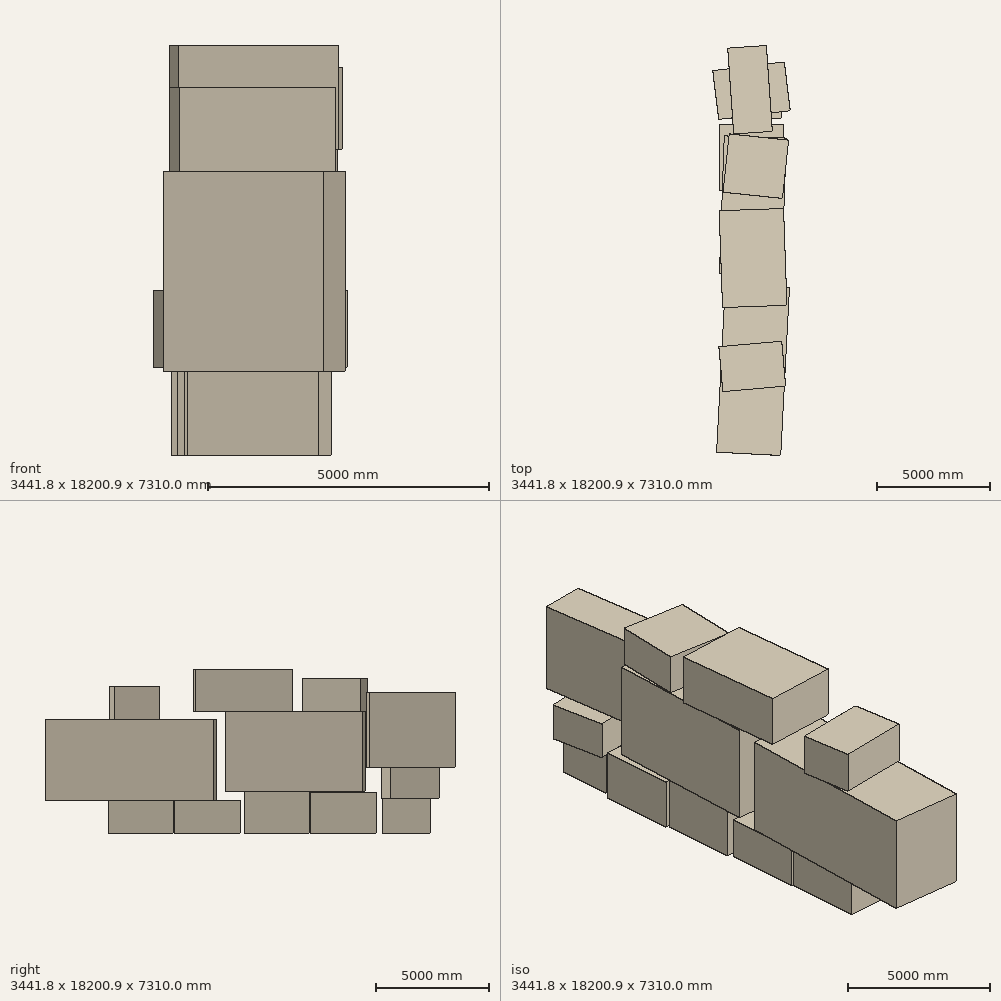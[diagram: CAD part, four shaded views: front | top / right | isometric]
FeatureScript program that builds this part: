
annotation { "Feature Type Name" : "Feature", "Feature Type Description" : "" }
export const myFeature = defineFeature(function(context is Context, id is Id, definition is map)
    precondition{}
    {
        {
            var Q0;
            Q0=qCreatedBy(makeId("Top.planeOp"),FACE);
            cPlane(context, id + "F0", {"entities" : qUnion([Q0]), "cplaneType" : CPlaneType.OFFSET, "offset" : 400 * mm, "width" : 150 * mm, "height" : 150 * mm});
        }
        {
            var Q0;
            Q0=qCreatedBy(id+"F0.planeOp",FACE);
            var sketch = newSketch(context, id + "F1", { "sketchPlane" : qUnion([Q0])});
            skLineSegment(sketch, "E0.bottom", {"start": v(-1230, 5840) * mm, "end": v(1110, 5840) * mm});
            skLineSegment(sketch, "E0.top", {"start": v(-1230, 2940) * mm, "end": v(1110, 2940) * mm});
            skLineSegment(sketch, "E0.left", {"start": v(-1230, 5840) * mm, "end": v(-1230, 2940) * mm});
            skLineSegment(sketch, "E0.right", {"start": v(1110, 5840) * mm, "end": v(1110, 2940) * mm});
            skLineSegment(sketch, "E1.bottom", {"start": v(-1170, 2900) * mm, "end": v(1170, 2900) * mm});
            skLineSegment(sketch, "E1.top", {"start": v(-1170, 0) * mm, "end": v(1170, 0) * mm});
            skLineSegment(sketch, "E1.left", {"start": v(-1170, 2900) * mm, "end": v(-1170, 0) * mm});
            skLineSegment(sketch, "E1.right", {"start": v(1170, 2900) * mm, "end": v(1170, 0) * mm});
            skLineSegment(sketch, "E2.bottom", {"start": v(-1350, 6020) * mm, "end": v(1170, 6020) * mm});
            skLineSegment(sketch, "E2.top", {"start": v(-1350, 8920) * mm, "end": v(1170, 8920) * mm});
            skLineSegment(sketch, "E2.left", {"start": v(-1350, 6020) * mm, "end": v(-1350, 8920) * mm});
            skLineSegment(sketch, "E2.right", {"start": v(1170, 6020) * mm, "end": v(1170, 8920) * mm});
            skLineSegment(sketch, "E3.bottom", {"start": v(-1450, 11880) * mm, "end": v(1390, 11880) * mm});
            skLineSegment(sketch, "E3.top", {"start": v(-1450, 8980) * mm, "end": v(1390, 8980) * mm});
            skLineSegment(sketch, "E3.left", {"start": v(-1450, 11880) * mm, "end": v(-1450, 8980) * mm});
            skLineSegment(sketch, "E3.right", {"start": v(1390, 11880) * mm, "end": v(1390, 8980) * mm});
            skLineSegment(sketch, "E4.bottom", {"start": v(1290, 12180) * mm, "end": v(0, 12180) * mm});
            skLineSegment(sketch, "E4.top", {"start": v(1290, 14280) * mm, "end": v(0, 14280) * mm});
            skLineSegment(sketch, "E4.left", {"start": v(1290, 12180) * mm, "end": v(1290, 14280) * mm});
            skLineSegment(sketch, "E4.right", {"start": v(0, 12180) * mm, "end": v(0, 14280) * mm});
            skLineSegment(sketch, "E5.bottom", {"start": v(-1240, 14280) * mm, "end": v(-50, 14280) * mm});
            skLineSegment(sketch, "E5.top", {"start": v(-1240, 12180) * mm, "end": v(-50, 12180) * mm});
            skLineSegment(sketch, "E5.left", {"start": v(-1240, 14280) * mm, "end": v(-1240, 12180) * mm});
            skLineSegment(sketch, "E5.right", {"start": v(-50, 14280) * mm, "end": v(-50, 12180) * mm});
            skSolve(sketch);
        }
        {
            var Q0;
            Q0=makeQuery(id+"F1.imprint","IMPRINT",FACE,{"disambiguationData":[TD([[makeQuery(id+"F1.imprint","IMPRINT",EDGE,{"derivedFrom":sQuery(id+"F1.wireOp",EDGE,"E1.bottom")}),-1.0]])]});
            var Q1;
            Q1=makeQuery(id+"F1.imprint","IMPRINT",FACE,{"disambiguationData":[TD([[makeQuery(id+"F1.imprint","IMPRINT",EDGE,{"derivedFrom":sQuery(id+"F1.wireOp",EDGE,"E0.bottom")}),-1.0]])]});
            extrude(context, id + "F2", {"entities" : qUnion([Q0, Q1]), "depth" : 1500 * mm, "offsetDistance" : 25 * mm});
        }
        {
            var Q0;
            Q0=makeQuery(id+"F1.imprint","IMPRINT",FACE,{"disambiguationData":[TD([[makeQuery(id+"F1.imprint","IMPRINT",EDGE,{"derivedFrom":sQuery(id+"F1.wireOp",EDGE,"E2.bottom")}),1.0]])]});
            extrude(context, id + "F3", {"entities" : qUnion([Q0]), "depth" : 1900 * mm, "offsetDistance" : 25 * mm});
        }
        {
            var Q0;
            Q0=makeQuery(id+"F1.imprint","IMPRINT",FACE,{"disambiguationData":[TD([[makeQuery(id+"F1.imprint","IMPRINT",EDGE,{"derivedFrom":sQuery(id+"F1.wireOp",EDGE,"E3.bottom")}),-1.0]])]});
            extrude(context, id + "F4", {"entities" : qUnion([Q0]), "depth" : 1840 * mm, "offsetDistance" : 25 * mm});
        }
        {
            var Q0;
            Q0=makeQuery(id+"F1.imprint","IMPRINT",FACE,{"disambiguationData":[TD([[makeQuery(id+"F1.imprint","IMPRINT",EDGE,{"derivedFrom":sQuery(id+"F1.wireOp",EDGE,"E5.bottom")}),-1.0]])]});
            var Q1;
            Q1=makeQuery(id+"F1.imprint","IMPRINT",FACE,{"disambiguationData":[TD([[makeQuery(id+"F1.imprint","IMPRINT",EDGE,{"derivedFrom":sQuery(id+"F1.wireOp",EDGE,"E4.bottom")}),-1.0]])]});
            extrude(context, id + "F5", {"entities" : qUnion([Q0, Q1]), "depth" : 1570 * mm, "offsetDistance" : 25 * mm});
        }
        {
            var Q0;
            Q0=makeQuery(id+"F2.opExtrude","CAP_FACE",FACE,{"disambiguationData":[OSD([sQuery(id+"F1.wireOp",EDGE,"E1.bottom"),sQuery(id+"F1.wireOp",EDGE,"E1.top"),sQuery(id+"F1.wireOp",EDGE,"E1.left"),sQuery(id+"F1.wireOp",EDGE,"E1.right")])],"isStart":false});
            var sketch = newSketch(context, id + "F6", { "sketchPlane" : qUnion([Q0])});
            skLineSegment(sketch, "E6", {"start": v(-1205.45, 4814.1) * mm, "end": v(-1596.4, -2645.66) * mm});
            skLineSegment(sketch, "E7", {"start": v(-1596.4, -2645.66) * mm, "end": v(1249.7, -2794.82) * mm});
            skLineSegment(sketch, "E8", {"start": v(1249.7, -2794.82) * mm, "end": v(1640.64, 4664.94) * mm});
            skLineSegment(sketch, "E9", {"start": v(1640.64, 4664.94) * mm, "end": v(-1205.45, 4814.1) * mm});
            skSolve(sketch);
        }
        {
            var Q0;
            Q0 = qSketchRegion(id + "F6", true);
            extrude(context, id + "F7", {"entities" : qUnion([Q0]), "depth" : 3560 * mm, "offsetDistance" : 25 * mm});
        }
        {
            var Q0;
            Q0=makeQuery(id+"F3.opExtrude","CAP_FACE",FACE,{"disambiguationData":[OSD([sQuery(id+"F1.wireOp",EDGE,"E2.bottom"),sQuery(id+"F1.wireOp",EDGE,"E2.top"),sQuery(id+"F1.wireOp",EDGE,"E2.left"),sQuery(id+"F1.wireOp",EDGE,"E2.right")])],"isStart":false});
            var sketch = newSketch(context, id + "F8", { "sketchPlane" : qUnion([Q0])});
            skLineSegment(sketch, "E10", {"start": v(-1256.52, 11393.39) * mm, "end": v(1501.8, 11297.06) * mm});
            skLineSegment(sketch, "E11", {"start": v(1501.8, 11297.06) * mm, "end": v(1288.9, 5200.78) * mm});
            skLineSegment(sketch, "E12", {"start": v(1288.9, 5200.78) * mm, "end": v(-1469.41, 5297.1) * mm});
            skLineSegment(sketch, "E13", {"start": v(-1469.41, 5297.1) * mm, "end": v(-1256.52, 11393.39) * mm});
            skSolve(sketch);
        }
        {
            var Q0;
            Q0 = qSketchRegion(id + "F8", true);
            extrude(context, id + "F9", {"entities" : qUnion([Q0]), "operationType" : NewBodyOperationType.ADD, "depth" : 3550 * mm, "offsetDistance" : 25 * mm});
        }
        {
            var Q0;
            Q0=makeQuery(id+"F5.opExtrude","CAP_FACE",FACE,{"disambiguationData":[OSD([sQuery(id+"F1.wireOp",EDGE,"E4.bottom"),sQuery(id+"F1.wireOp",EDGE,"E4.top"),sQuery(id+"F1.wireOp",EDGE,"E4.left"),sQuery(id+"F1.wireOp",EDGE,"E4.right")])],"isStart":false});
            var sketch = newSketch(context, id + "F10", { "sketchPlane" : qUnion([Q0])});
            skLineSegment(sketch, "E14", {"start": v(-1768.05, 14284.32) * mm, "end": v(-1502.38, 12120.57) * mm});
            skLineSegment(sketch, "E15", {"start": v(-1502.38, 12120.57) * mm, "end": v(1673.77, 12510.55) * mm});
            skLineSegment(sketch, "E16", {"start": v(1673.77, 12510.55) * mm, "end": v(1408.1, 14674.3) * mm});
            skLineSegment(sketch, "E17", {"start": v(1408.1, 14674.3) * mm, "end": v(-1768.05, 14284.32) * mm});
            skSolve(sketch);
        }
        {
            var Q0;
            Q0 = qSketchRegion(id + "F10", true);
            extrude(context, id + "F11", {"entities" : qUnion([Q0]), "depth" : 1370 * mm, "offsetDistance" : 25 * mm});
        }
        {
            var Q0;
            Q0=makeQuery(id+"F11.opExtrude","CAP_FACE",FACE,{"disambiguationData":[OSD([sQuery(id+"F10.wireOp",EDGE,"E14"),sQuery(id+"F10.wireOp",EDGE,"E15"),sQuery(id+"F10.wireOp",EDGE,"E16"),sQuery(id+"F10.wireOp",EDGE,"E17")])],"isStart":false});
            var sketch = newSketch(context, id + "F12", { "sketchPlane" : qUnion([Q0])});
            skLineSegment(sketch, "E18", {"start": v(-1103.8, 15286.1) * mm, "end": v(-837.33, 11475.4) * mm});
            skLineSegment(sketch, "E19", {"start": v(-837.33, 11475.4) * mm, "end": v(878.48, 11595.38) * mm});
            skLineSegment(sketch, "E20", {"start": v(878.48, 11595.38) * mm, "end": v(612.01, 15406.08) * mm});
            skLineSegment(sketch, "E21", {"start": v(612.01, 15406.08) * mm, "end": v(-1103.8, 15286.1) * mm});
            skSolve(sketch);
        }
        {
            var Q0;
            Q0 = qSketchRegion(id + "F12", true);
            extrude(context, id + "F13", {"entities" : qUnion([Q0]), "operationType" : NewBodyOperationType.ADD, "depth" : 3320 * mm, "offsetDistance" : 25 * mm});
        }
        {
            var Q0;
            Q0=makeQuery(id+"F7.opExtrude","CAP_FACE",FACE,{"disambiguationData":[OSD([sQuery(id+"F6.wireOp",EDGE,"E6"),sQuery(id+"F6.wireOp",EDGE,"E7"),sQuery(id+"F6.wireOp",EDGE,"E8"),sQuery(id+"F6.wireOp",EDGE,"E9")])],"isStart":false});
            var sketch = newSketch(context, id + "F14", { "sketchPlane" : qUnion([Q0])});
            skLineSegment(sketch, "E22", {"start": v(-1494.9, 2032.3) * mm, "end": v(-1320.6, 39.91) * mm});
            skLineSegment(sketch, "E23", {"start": v(-1320.6, 39.91) * mm, "end": v(1468.75, 283.95) * mm});
            skLineSegment(sketch, "E24", {"start": v(1468.75, 283.95) * mm, "end": v(1294.44, 2276.34) * mm});
            skLineSegment(sketch, "E25", {"start": v(1294.44, 2276.34) * mm, "end": v(-1494.9, 2032.3) * mm});
            skSolve(sketch);
        }
        {
            var Q0;
            Q0 = qSketchRegion(id + "F14", true);
            extrude(context, id + "F15", {"entities" : qUnion([Q0]), "operationType" : NewBodyOperationType.ADD, "depth" : 1500 * mm, "offsetDistance" : 25 * mm});
        }
        {
            var Q0;
            Q0=makeQuery(id+"F9.opExtrude","CAP_FACE",FACE,{"disambiguationData":[OSD([sQuery(id+"F8.wireOp",EDGE,"E10"),sQuery(id+"F8.wireOp",EDGE,"E11"),sQuery(id+"F8.wireOp",EDGE,"E12"),sQuery(id+"F8.wireOp",EDGE,"E13")])],"isStart":false});
            var sketch = newSketch(context, id + "F16", { "sketchPlane" : qUnion([Q0])});
            skLineSegment(sketch, "E26", {"start": v(-1483.18, 8070.12) * mm, "end": v(-1333.12, 3772.74) * mm});
            skLineSegment(sketch, "E27", {"start": v(-1333.12, 3772.74) * mm, "end": v(1525.14, 3872.55) * mm});
            skLineSegment(sketch, "E28", {"start": v(1525.14, 3872.55) * mm, "end": v(1375.07, 8169.93) * mm});
            skLineSegment(sketch, "E29", {"start": v(1375.07, 8169.93) * mm, "end": v(-1483.18, 8070.12) * mm});
            skLineSegment(sketch, "E30", {"start": v(-1035.12, 11480.63) * mm, "end": v(1600.36, 11203.63) * mm});
            skLineSegment(sketch, "E31", {"start": v(1600.36, 11203.63) * mm, "end": v(1328.59, 8617.87) * mm});
            skLineSegment(sketch, "E32", {"start": v(1328.59, 8617.87) * mm, "end": v(-1306.9, 8894.87) * mm});
            skLineSegment(sketch, "E33", {"start": v(-1306.9, 8894.87) * mm, "end": v(-1035.12, 11480.63) * mm});
            skSolve(sketch);
        }
        {
            var Q0;
            {var subQ7=sQuery(id+"F16.wireOp",EDGE,"E26");var subQ8=makeQuery(id+"F9.opExtrude","CAP_EDGE",EDGE,{"disambiguationData":[OSD([sQuery(id+"F8.wireOp",EDGE,"E13")])],"isStart":false});var subQ9=makeQuery(id+"F16.imprint","INTERSECT",VERTEX,{"derivedFrom":[subQ8,subQ7]});Q0=makeQuery(id+"F16.imprint","IMPRINT",FACE,{"disambiguationData":[TD([[makeQuery(id+"F16.imprint","IMPRINT",EDGE,{"disambiguationData":[TD([[subQ9,-1.0]])],"derivedFrom":subQ7}),1.0]])]});}
            var Q1;
            {var subQ5=sQuery(id+"F16.wireOp",EDGE,"E27");Q1=makeQuery(id+"F16.imprint","IMPRINT",FACE,{"disambiguationData":[TD([[makeQuery(id+"F16.imprint","IMPRINT",EDGE,{"derivedFrom":subQ5}),1.0]])]});}
            var Q2;
            {var subQ0=sQuery(id+"F16.wireOp",EDGE,"E29");var subQ1=sQuery(id+"F16.wireOp",EDGE,"E26");var subQ2=makeQuery(id+"F16.imprint","INTERSECT",VERTEX,{"derivedFrom":[subQ1,subQ0]});Q2=makeQuery(id+"F16.imprint","IMPRINT",FACE,{"disambiguationData":[TD([[makeQuery(id+"F16.imprint","IMPRINT",EDGE,{"disambiguationData":[TD([[subQ2,-1.0]])],"derivedFrom":subQ1}),1.0]])]});}
            extrude(context, id + "F17", {"entities" : qUnion([Q0, Q1, Q2]), "operationType" : NewBodyOperationType.ADD, "depth" : 1860 * mm, "offsetDistance" : 25 * mm});
        }
        {
            var Q0;
            {var subQ0=sQuery(id+"F16.wireOp",EDGE,"E31");var subQ1=sQuery(id+"F16.wireOp",EDGE,"E30");var subQ2=makeQuery(id+"F16.imprint","INTERSECT",VERTEX,{"derivedFrom":[subQ1,subQ0]});Q0=makeQuery(id+"F16.imprint","IMPRINT",FACE,{"disambiguationData":[TD([[makeQuery(id+"F16.imprint","IMPRINT",EDGE,{"disambiguationData":[TD([[subQ2,1.0]])],"derivedFrom":subQ1}),-1.0]])]});}
            var Q1;
            {var subQ0=sQuery(id+"F16.wireOp",EDGE,"E32");Q1=makeQuery(id+"F16.imprint","IMPRINT",FACE,{"disambiguationData":[TD([[makeQuery(id+"F16.imprint","IMPRINT",EDGE,{"derivedFrom":subQ0}),-1.0]])]});}
            var Q2;
            {var subQ0=sQuery(id+"F16.wireOp",EDGE,"E33");var subQ1=sQuery(id+"F16.wireOp",EDGE,"E30");var subQ2=makeQuery(id+"F16.imprint","INTERSECT",VERTEX,{"derivedFrom":[subQ1,subQ0]});Q2=makeQuery(id+"F16.imprint","IMPRINT",FACE,{"disambiguationData":[TD([[makeQuery(id+"F16.imprint","IMPRINT",EDGE,{"disambiguationData":[TD([[subQ2,-1.0]])],"derivedFrom":subQ1}),-1.0]])]});}
            extrude(context, id + "F18", {"entities" : qUnion([Q0, Q1, Q2]), "operationType" : NewBodyOperationType.ADD, "depth" : 1460 * mm, "offsetDistance" : 25 * mm});
        }
    });
